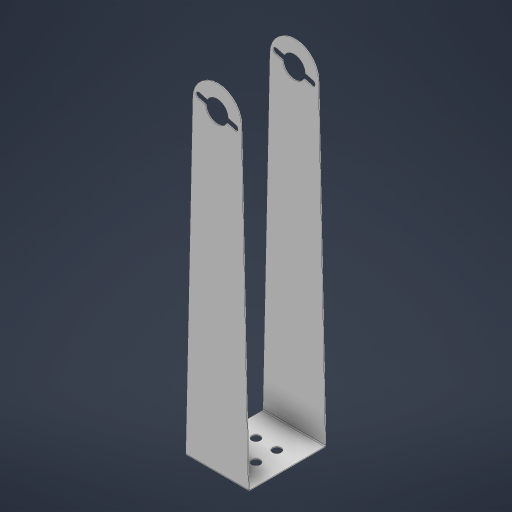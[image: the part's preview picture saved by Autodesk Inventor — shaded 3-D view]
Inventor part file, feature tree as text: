
AUTODESK INVENTOR PART (.ipt)
format: ipt  version: 2024 (Build 280153000, 153)  size: 267,776 bytes
history: native  units: mm
features: other x5, sketch x2
ambient origin geometry x8: Origin, YZ Plane, XZ Plane, XY Plane, X Axis, Y Axis, Z Axis, Center Point
bodies: Body1 (feature_tree)
feature tree (7):
  other  "Sólido1"
  sketch  "Boceto1"  dims[d3=18.0mm]
  other  "Cara1"
  other  "Pliegue1"
  other  "Pliegue2"
  sketch  "Boceto2"  dims[d7=5.0mm d8=6.0mm d9=6.0mm d10=40.0mm d12=360.0deg d14=14.0mm d15=180.0mm d16=0.5mm d17=0.5mm d18=0.25mm d19=1.0mm d20=0.5mm d21=90.0deg d22=0.5mm d23=0.5mm d24=0.25mm d25=1.0mm d26=0.5mm d27=90.0deg d28=0.5mm]
  other  "Placa1"
